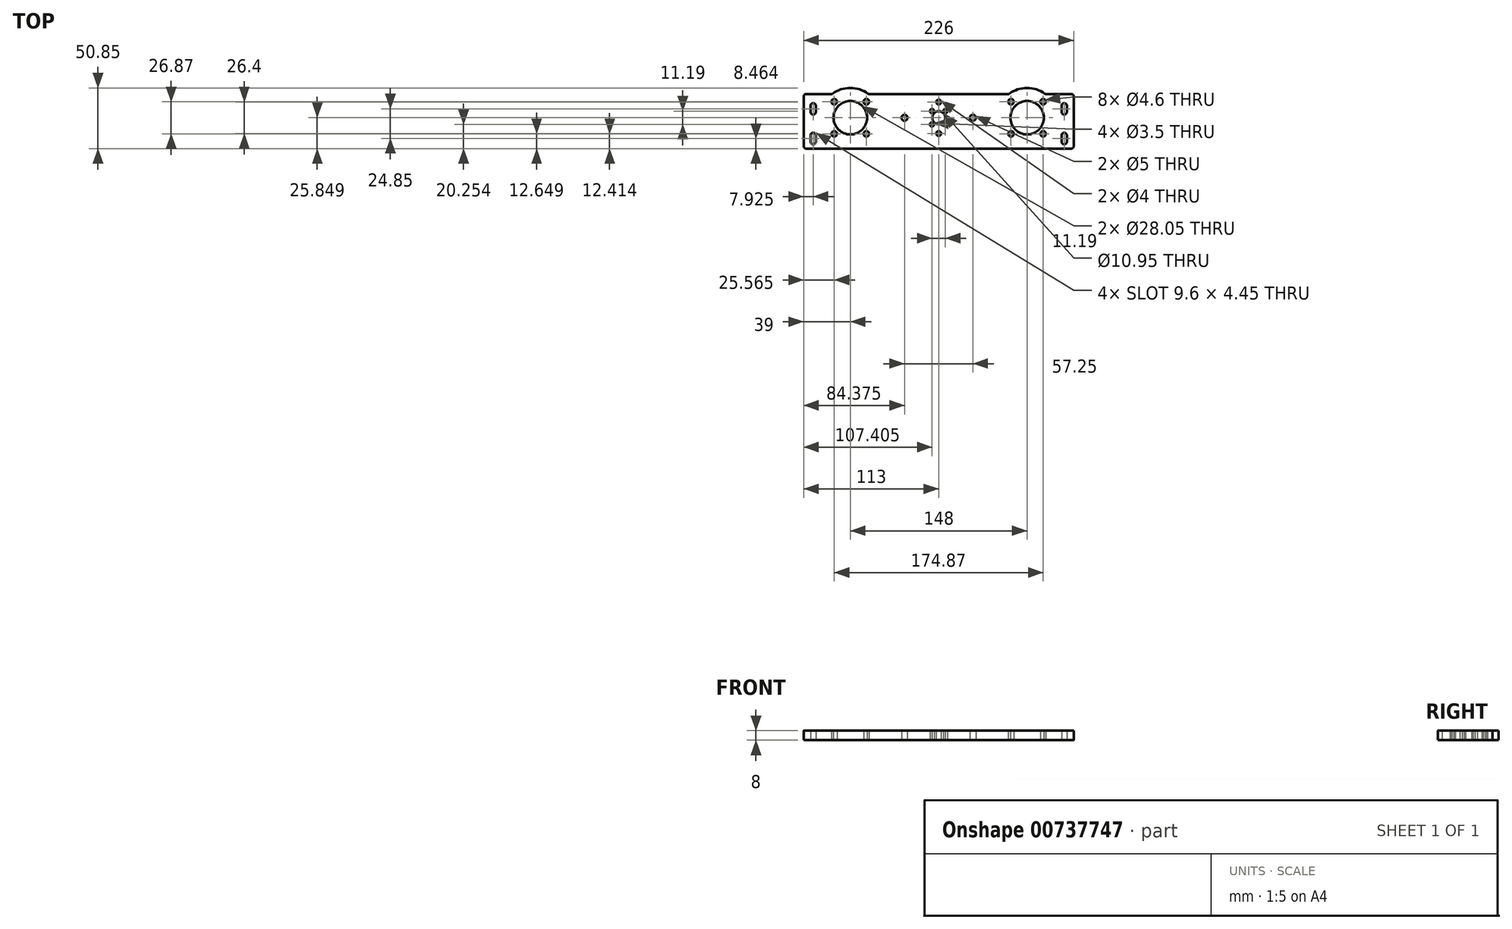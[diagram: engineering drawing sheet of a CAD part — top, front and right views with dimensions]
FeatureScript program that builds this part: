
annotation { "Feature Type Name" : "Feature", "Feature Type Description" : "" }
export const myFeature = defineFeature(function(context is Context, id is Id, definition is map)
    precondition{}
    {
        {
            var Q0;
            Q0=qCreatedBy(makeId("Top.planeOp"),FACE);
            var sketch = newSketch(context, id + "F0", { "sketchPlane" : qUnion([Q0])});
            skLineSegment(sketch, "E0.bottom", {"start": v(-109.95, 1.5) * mm, "end": v(-88.38, 1.5) * mm});
            skLineSegment(sketch, "E0.left", {"start": v(-111.95, -0.5) * mm, "end": v(-111.95, -42.27) * mm});
            skLineSegment(sketch, "E0.right", {"start": v(114.05, -0.5) * mm, "end": v(114.05, -42.27) * mm});
            skLineSegment(sketch, "E1", {"start": v(1.05, 1.5) * mm, "end": v(1.05, -48.27) * mm, "construction": true});
            skCircle(sketch, "E2", {"center": v(1.05, -18.42) * mm, "radius": 5.47 * mm});
            skLineSegment(sketch, "E3", {"start": v(-111.95, -18.42) * mm, "end": v(114.05, -18.42) * mm, "construction": true});
            skPoint(sketch, "E3.endSnap0", {"position": v(114.05, -23.38) * mm});
            skCircle(sketch, "E4", {"center": v(75.05, -18.42) * mm, "radius": 14.03 * mm});
            skLineSegment(sketch, "E5", {"start": v(106.13, 1.5) * mm, "end": v(106.13, -48.27) * mm, "construction": true});
            skArc(sketch, "E6", {"start": v(108.35, -8.38) * mm, "mid": v(106.13, -6.16) * mm, "end": v(103.9, -8.38) * mm});
            skArc(sketch, "E7", {"start": v(103.9, -13.53) * mm, "mid": v(106.13, -15.76) * mm, "end": v(108.35, -13.53) * mm});
            skLineSegment(sketch, "E8", {"start": v(114.05, -23.38) * mm, "end": v(-111.95, -23.38) * mm, "construction": true});
            skLineSegment(sketch, "E9", {"start": v(103.9, -8.38) * mm, "end": v(108.35, -8.38) * mm, "construction": true});
            skLineSegment(sketch, "E10", {"start": v(103.9, -13.53) * mm, "end": v(108.35, -13.53) * mm, "construction": true});
            skLineSegment(sketch, "E11", {"start": v(103.9, -8.38) * mm, "end": v(103.9, -13.53) * mm});
            skLineSegment(sketch, "E12", {"start": v(108.35, -8.38) * mm, "end": v(108.35, -13.53) * mm});
            skArc(sketch, "E13.MirrorCS", {"start": v(103.9, -33.23) * mm, "mid": v(106.13, -31) * mm, "end": v(108.35, -33.23) * mm});
            skLineSegment(sketch, "E14.MirrorCS", {"start": v(103.9, -38.38) * mm, "end": v(103.9, -33.23) * mm});
            skLineSegment(sketch, "E15.MirrorCS", {"start": v(108.35, -38.38) * mm, "end": v(108.35, -33.23) * mm});
            skArc(sketch, "E16.MirrorCS", {"start": v(108.35, -38.38) * mm, "mid": v(106.13, -40.6) * mm, "end": v(103.9, -38.38) * mm});
            skLineSegment(sketch, "E17.MirrorCS", {"start": v(-101.8, -38.38) * mm, "end": v(-101.8, -33.23) * mm});
            skArc(sketch, "E18.MirrorCS", {"start": v(-106.25, -38.38) * mm, "mid": v(-104.02, -40.6) * mm, "end": v(-101.8, -38.38) * mm});
            skLineSegment(sketch, "E19.MirrorCS", {"start": v(-106.25, -38.38) * mm, "end": v(-106.25, -33.23) * mm});
            skArc(sketch, "E20.MirrorCS", {"start": v(-101.8, -33.23) * mm, "mid": v(-104.02, -31) * mm, "end": v(-106.25, -33.23) * mm});
            skLineSegment(sketch, "E21.MirrorCS", {"start": v(-101.8, -13.53) * mm, "end": v(-106.25, -13.53) * mm, "construction": true});
            skLineSegment(sketch, "E22.MirrorCS", {"start": v(-104.02, 1.5) * mm, "end": v(-104.02, -48.27) * mm, "construction": true});
            skLineSegment(sketch, "E23.MirrorCS", {"start": v(-101.8, -8.38) * mm, "end": v(-106.25, -8.38) * mm, "construction": true});
            skLineSegment(sketch, "E24.MirrorCS", {"start": v(-106.25, -8.38) * mm, "end": v(-106.25, -13.53) * mm});
            skArc(sketch, "E25.MirrorCS", {"start": v(-106.25, -8.38) * mm, "mid": v(-104.02, -6.16) * mm, "end": v(-101.8, -8.38) * mm});
            skLineSegment(sketch, "E26.MirrorCS", {"start": v(-101.8, -8.38) * mm, "end": v(-101.8, -13.53) * mm});
            skArc(sketch, "E27.MirrorCS", {"start": v(-101.8, -13.53) * mm, "mid": v(-104.02, -15.76) * mm, "end": v(-106.25, -13.53) * mm});
            skLineSegment(sketch, "E28", {"start": v(75.05, -18.42) * mm, "end": v(88.49, -31.86) * mm, "construction": true});
            skCircle(sketch, "E29", {"center": v(88.49, -31.86) * mm, "radius": 2.3 * mm});
            skCircle(sketch, "E30.1.0", {"center": v(88.49, -4.99) * mm, "radius": 2.3 * mm});
            skCircle(sketch, "E30.2.0", {"center": v(61.62, -4.99) * mm, "radius": 2.3 * mm});
            skCircle(sketch, "E30.3.0", {"center": v(61.62, -31.86) * mm, "radius": 2.3 * mm});
            skCircle(sketch, "E31.MirrorC", {"center": v(-72.95, -18.42) * mm, "radius": 14.03 * mm});
            skCircle(sketch, "E32.MirrorC", {"center": v(-86.38, -31.86) * mm, "radius": 2.3 * mm});
            skCircle(sketch, "E33.MirrorC", {"center": v(-59.51, -31.86) * mm, "radius": 2.3 * mm});
            skCircle(sketch, "E34.MirrorC", {"center": v(-59.51, -4.99) * mm, "radius": 2.3 * mm});
            skCircle(sketch, "E35.MirrorC", {"center": v(-86.38, -4.99) * mm, "radius": 2.3 * mm});
            skLineSegment(sketch, "E36", {"start": v(1.05, -18.42) * mm, "end": v(6.53, -18.42) * mm, "construction": true});
            skLineSegment(sketch, "E37", {"start": v(1.05, -18.42) * mm, "end": v(6.65, -24.02) * mm, "construction": true});
            skCircle(sketch, "E38", {"center": v(6.65, -24.02) * mm, "radius": 1.75 * mm});
            skCircle(sketch, "E39.1.0", {"center": v(6.65, -12.83) * mm, "radius": 1.75 * mm});
            skCircle(sketch, "E39.2.0", {"center": v(-4.54, -12.83) * mm, "radius": 1.75 * mm});
            skCircle(sketch, "E39.3.0", {"center": v(-4.54, -24.02) * mm, "radius": 1.75 * mm});
            skPoint(sketch, "E40.visualSharp", {"position": v(-111.95, 1.5) * mm});
            skArc(sketch, "E40.filletArc", {"start": v(-109.95, 1.5) * mm, "mid": v(-111.36, 0.92) * mm, "end": v(-111.95, -0.5) * mm});
            skPoint(sketch, "E41.visualSharp", {"position": v(-111.95, -48.27) * mm});
            skPoint(sketch, "E42.visualSharp", {"position": v(114.05, 1.5) * mm});
            skArc(sketch, "E42.filletArc", {"start": v(114.05, -0.5) * mm, "mid": v(113.46, 0.92) * mm, "end": v(112.05, 1.5) * mm});
            skPoint(sketch, "E43.visualSharp", {"position": v(114.05, -48.27) * mm});
            skArc(sketch, "E44", {"start": v(-58.11, 1.7) * mm, "mid": v(-72.95, 6.58) * mm, "end": v(-87.79, 1.7) * mm});
            skLineSegment(sketch, "E45.trimOffspring", {"start": v(-57.52, 1.5) * mm, "end": v(59.62, 1.5) * mm});
            skLineSegment(sketch, "E46.trimOffspring", {"start": v(-84.72, -44.27) * mm, "end": v(86.82, -44.27) * mm});
            skArc(sketch, "E47.trimOffspring", {"start": v(89.89, 1.7) * mm, "mid": v(75.05, 6.58) * mm, "end": v(60.21, 1.7) * mm});
            skLineSegment(sketch, "E48.trimOffspring", {"start": v(90.48, 1.5) * mm, "end": v(112.05, 1.5) * mm});
            skPoint(sketch, "E49.visualSharp", {"position": v(-111.95, -69.27) * mm});
            skPoint(sketch, "E50.visualSharp", {"position": v(-95, -69.27) * mm});
            skPoint(sketch, "E51.visualSharp", {"position": v(-85.4, -44.27) * mm});
            skPoint(sketch, "E52.visualSharp", {"position": v(87.5, -44.27) * mm});
            skPoint(sketch, "E53.visualSharp", {"position": v(97.1, -69.27) * mm});
            skPoint(sketch, "E54.visualSharp", {"position": v(114.05, -69.27) * mm});
            skPoint(sketch, "E55.visualSharp", {"position": v(90.15, 1.5) * mm});
            skArc(sketch, "E55.filletArc", {"start": v(89.89, 1.7) * mm, "mid": v(90.17, 1.55) * mm, "end": v(90.48, 1.5) * mm});
            skPoint(sketch, "E56.visualSharp", {"position": v(59.95, 1.5) * mm});
            skArc(sketch, "E56.filletArc", {"start": v(59.62, 1.5) * mm, "mid": v(59.93, 1.55) * mm, "end": v(60.21, 1.7) * mm});
            skPoint(sketch, "E57.visualSharp", {"position": v(-57.85, 1.5) * mm});
            skArc(sketch, "E57.filletArc", {"start": v(-58.11, 1.7) * mm, "mid": v(-57.83, 1.55) * mm, "end": v(-57.52, 1.5) * mm});
            skPoint(sketch, "E58.visualSharp", {"position": v(-88.05, 1.5) * mm});
            skArc(sketch, "E58.filletArc", {"start": v(-88.38, 1.5) * mm, "mid": v(-88.07, 1.55) * mm, "end": v(-87.79, 1.7) * mm});
            skLineSegment(sketch, "E59", {"start": v(-84.72, -44.27) * mm, "end": v(-109.95, -44.27) * mm});
            skLineSegment(sketch, "E60", {"start": v(86.82, -44.27) * mm, "end": v(112.05, -44.27) * mm});
            skPoint(sketch, "E61.visualSharp", {"position": v(114.05, -44.27) * mm});
            skArc(sketch, "E61.filletArc", {"start": v(112.05, -44.27) * mm, "mid": v(113.46, -43.68) * mm, "end": v(114.05, -42.27) * mm});
            skPoint(sketch, "E62.visualSharp", {"position": v(-111.95, -44.27) * mm});
            skArc(sketch, "E62.filletArc", {"start": v(-111.95, -42.27) * mm, "mid": v(-111.36, -43.68) * mm, "end": v(-109.95, -44.27) * mm});
            skCircle(sketch, "E63", {"center": v(1.05, -5.22) * mm, "radius": 2 * mm});
            skCircle(sketch, "E64", {"center": v(1.05, -31.62) * mm, "radius": 2 * mm});
            skCircle(sketch, "E65", {"center": v(-27.57, -18.42) * mm, "radius": 2.5 * mm});
            skCircle(sketch, "E66", {"center": v(29.68, -18.42) * mm, "radius": 2.5 * mm});
            skSolve(sketch);
        }
        {
            var Q0;
            Q0=makeQuery(id+"F0.imprint","IMPRINT",FACE,{"disambiguationData":[TD([[makeQuery(id+"F0.imprint","IMPRINT",EDGE,{"derivedFrom":sQuery(id+"F0.wireOp",EDGE,"E0.bottom")}),-1.0]])]});
            extrude(context, id + "F1", {"entities" : qUnion([Q0]), "depth" : 8 * mm, "offsetDistance" : 25 * mm});
        }
    });
